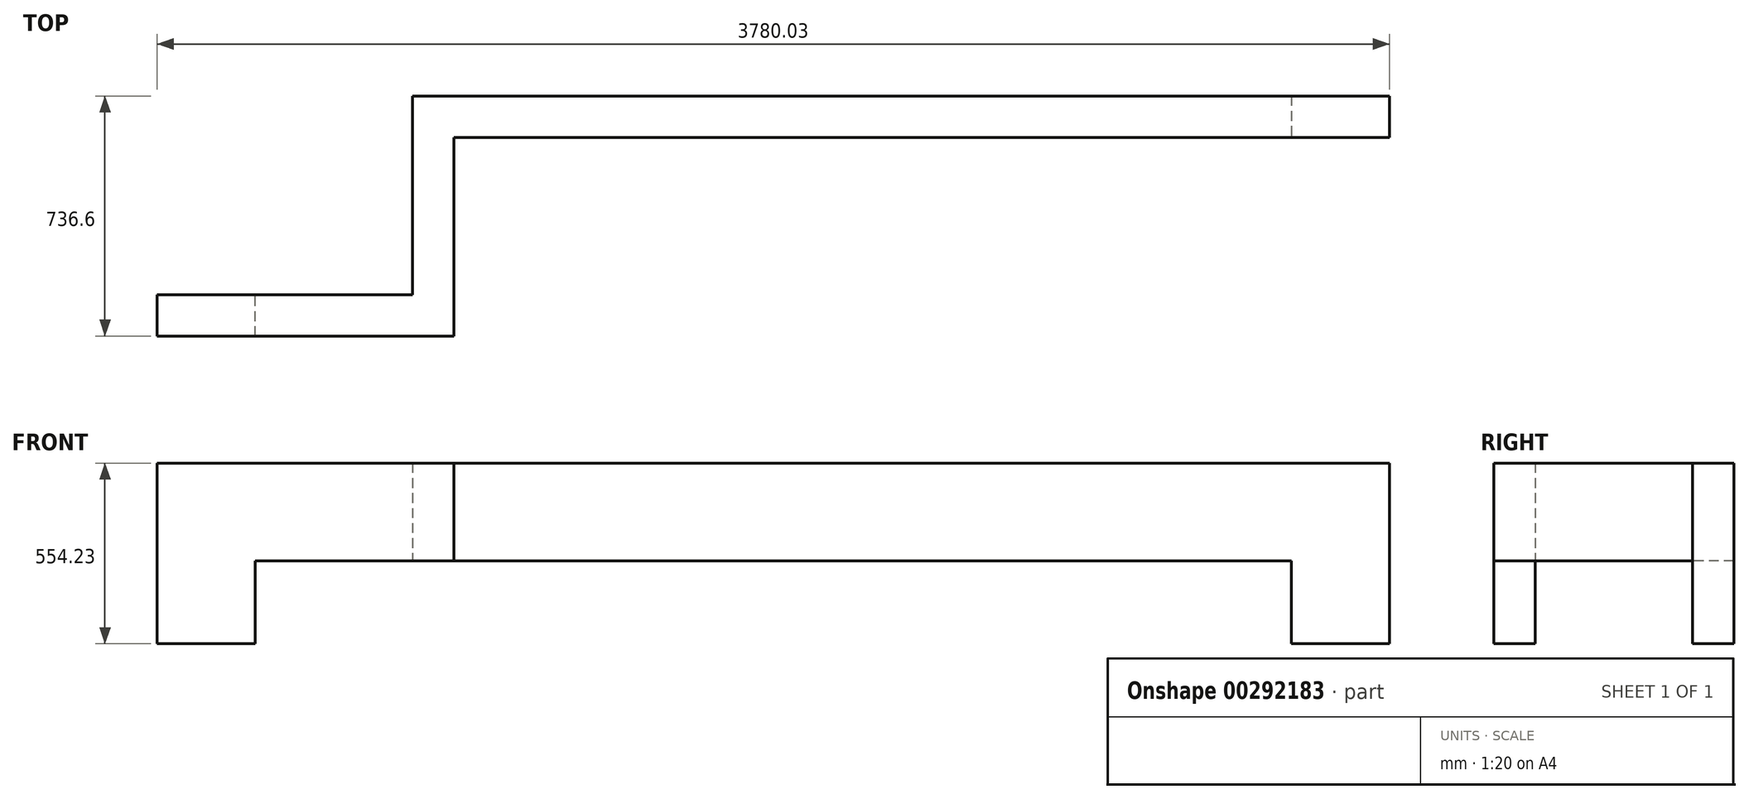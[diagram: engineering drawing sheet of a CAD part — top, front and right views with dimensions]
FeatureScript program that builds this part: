
annotation { "Feature Type Name" : "Feature", "Feature Type Description" : "" }
export const myFeature = defineFeature(function(context is Context, id is Id, definition is map)
    precondition{}
    {
        {
            var Q0;
            Q0=qCreatedBy(makeId("Top.planeOp"),FACE);
            var sketch = newSketch(context, id + "F0", { "sketchPlane" : qUnion([Q0])});
            skLineSegment(sketch, "E0.bottom", {"start": v(0, 0) * mm, "end": v(300.23, 0) * mm});
            skLineSegment(sketch, "E0.top", {"start": v(0, 127) * mm, "end": v(300.23, 127) * mm});
            skLineSegment(sketch, "E0.left", {"start": v(0, 0) * mm, "end": v(0, 127) * mm});
            skLineSegment(sketch, "E0.right", {"start": v(300.23, 0) * mm, "end": v(300.23, 127) * mm});
            skSolve(sketch);
        }
        {
            var Q0;
            Q0=makeQuery(id+"F0.imprint","IMPRINT",FACE,{"disambiguationData":[TD([[makeQuery(id+"F0.imprint","IMPRINT",EDGE,{"derivedFrom":sQuery(id+"F0.wireOp",EDGE,"E0.bottom")}),1.0]])]});
            extrude(context, id + "F1", {"entities" : qUnion([Q0]), "depth" : 254 * mm});
        }
        {
            var Q0;
            Q0=makeQuery(id+"F1.opExtrude","CAP_FACE",FACE,{"disambiguationData":[OSD([sQuery(id+"F0.wireOp",EDGE,"E0.bottom"),sQuery(id+"F0.wireOp",EDGE,"E0.top"),sQuery(id+"F0.wireOp",EDGE,"E0.left"),sQuery(id+"F0.wireOp",EDGE,"E0.right")])],"isStart":false});
            extrude(context, id + "F2", {"entities" : qUnion([Q0]), "operationType" : NewBodyOperationType.ADD, "depth" : 150.11 * mm});
        }
        {
            var Q0;
            Q0=makeQuery(id+"F2.opExtrude","CAP_FACE",FACE,{"disambiguationData":[OSD([sQuery(id+"F0.wireOp",EDGE,"E0.bottom"),sQuery(id+"F0.wireOp",EDGE,"E0.top"),sQuery(id+"F0.wireOp",EDGE,"E0.left"),sQuery(id+"F0.wireOp",EDGE,"E0.right")])],"isStart":false});
            extrude(context, id + "F3", {"entities" : qUnion([Q0]), "operationType" : NewBodyOperationType.ADD, "depth" : 150.11 * mm});
        }
        {
            var Q0;
            {var subQ0=sQuery(id+"F0.wireOp",EDGE,"E0.right");Q0=makeQuery(id+"F3.boolean.opBoolean","MERGE",FACE,{"derivedFrom":[makeQuery(id+"F2.boolean.opBoolean","MERGE",FACE,{"derivedFrom":[makeQuery(id+"F1.opExtrude","SWEPT_FACE",FACE,{"disambiguationData":[OSD([subQ0])]}),makeQuery(id+"F2.opExtrude","SWEPT_FACE",FACE,{"disambiguationData":[OSD([subQ0])]})]}),makeQuery(id+"F3.opExtrude","SWEPT_FACE",FACE,{"disambiguationData":[OSD([subQ0])]})]});}
            var sketch = newSketch(context, id + "F4", { "sketchPlane" : qUnion([Q0])});
            skLineSegment(sketch, "E1.bottom", {"start": v(0, 554.23) * mm, "end": v(127, 554.23) * mm});
            skLineSegment(sketch, "E1.top", {"start": v(0, 254) * mm, "end": v(127, 254) * mm});
            skLineSegment(sketch, "E1.left", {"start": v(0, 554.23) * mm, "end": v(0, 254) * mm});
            skLineSegment(sketch, "E1.right", {"start": v(127, 554.23) * mm, "end": v(127, 254) * mm});
            skSolve(sketch);
        }
        {
            var Q0;
            Q0=makeQuery(id+"F4.imprint","IMPRINT",FACE,{"disambiguationData":[TD([[makeQuery(id+"F4.imprint","IMPRINT",EDGE,{"derivedFrom":sQuery(id+"F4.wireOp",EDGE,"E1.bottom")}),-1.0]])]});
            extrude(context, id + "F5", {"entities" : qUnion([Q0]), "operationType" : NewBodyOperationType.ADD, "depth" : 609.6 * mm});
        }
        {
            var Q0;
            {var subQ0=sQuery(id+"F0.wireOp",EDGE,"E0.top");Q0=makeQuery(id+"F5.boolean.opBoolean","MERGE",FACE,{"derivedFrom":[makeQuery(id+"F3.boolean.opBoolean","MERGE",FACE,{"derivedFrom":[makeQuery(id+"F2.boolean.opBoolean","MERGE",FACE,{"derivedFrom":[makeQuery(id+"F1.opExtrude","SWEPT_FACE",FACE,{"disambiguationData":[OSD([subQ0])]}),makeQuery(id+"F2.opExtrude","SWEPT_FACE",FACE,{"disambiguationData":[OSD([subQ0])]})]}),makeQuery(id+"F3.opExtrude","SWEPT_FACE",FACE,{"disambiguationData":[OSD([subQ0])]})]}),makeQuery(id+"F5.opExtrude","SWEPT_FACE",FACE,{"disambiguationData":[OSD([sQuery(id+"F4.wireOp",EDGE,"E1.right")])]})]});}
            var sketch = newSketch(context, id + "F6", { "sketchPlane" : qUnion([Q0])});
            skLineSegment(sketch, "E2.bottom", {"start": v(-909.83, 554.23) * mm, "end": v(-782.83, 554.23) * mm});
            skLineSegment(sketch, "E2.top", {"start": v(-909.83, 254) * mm, "end": v(-782.83, 254) * mm});
            skLineSegment(sketch, "E2.left", {"start": v(-909.83, 554.23) * mm, "end": v(-909.83, 254) * mm});
            skLineSegment(sketch, "E2.right", {"start": v(-782.83, 554.23) * mm, "end": v(-782.83, 254) * mm});
            skSolve(sketch);
        }
        {
            var Q0;
            Q0=makeQuery(id+"F6.imprint","IMPRINT",FACE,{"disambiguationData":[TD([[makeQuery(id+"F6.imprint","IMPRINT",EDGE,{"derivedFrom":sQuery(id+"F6.wireOp",EDGE,"E2.bottom")}),1.0]])]});
            extrude(context, id + "F7", {"entities" : qUnion([Q0]), "operationType" : NewBodyOperationType.ADD, "depth" : 508 * mm});
        }
        {
            var Q0;
            Q0=makeQuery(id+"F7.boolean.opBoolean","MERGE",FACE,{"derivedFrom":[makeQuery(id+"F5.opExtrude","CAP_FACE",FACE,{"disambiguationData":[OSD([sQuery(id+"F4.wireOp",EDGE,"E1.bottom"),sQuery(id+"F4.wireOp",EDGE,"E1.top"),sQuery(id+"F4.wireOp",EDGE,"E1.left"),sQuery(id+"F4.wireOp",EDGE,"E1.right")])],"isStart":false}),makeQuery(id+"F7.opExtrude","SWEPT_FACE",FACE,{"disambiguationData":[OSD([sQuery(id+"F6.wireOp",EDGE,"E2.left")])]})]});
            var sketch = newSketch(context, id + "F8", { "sketchPlane" : qUnion([Q0])});
            skLineSegment(sketch, "E3.bottom", {"start": v(635, 554.23) * mm, "end": v(508, 554.23) * mm});
            skLineSegment(sketch, "E3.top", {"start": v(635, 254) * mm, "end": v(508, 254) * mm});
            skLineSegment(sketch, "E3.left", {"start": v(635, 554.23) * mm, "end": v(635, 254) * mm});
            skLineSegment(sketch, "E3.right", {"start": v(508, 554.23) * mm, "end": v(508, 254) * mm});
            skSolve(sketch);
        }
        {
            var Q0;
            Q0=makeQuery(id+"F8.imprint","IMPRINT",FACE,{"disambiguationData":[TD([[makeQuery(id+"F8.imprint","IMPRINT",EDGE,{"derivedFrom":sQuery(id+"F8.wireOp",EDGE,"E3.bottom")}),-1.0]])]});
            extrude(context, id + "F9", {"entities" : qUnion([Q0]), "operationType" : NewBodyOperationType.ADD, "depth" : 1524 * mm});
        }
        {
            var Q0;
            Q0=makeQuery(id+"F9.opExtrude","CAP_FACE",FACE,{"disambiguationData":[OSD([sQuery(id+"F8.wireOp",EDGE,"E3.bottom"),sQuery(id+"F8.wireOp",EDGE,"E3.top"),sQuery(id+"F8.wireOp",EDGE,"E3.left"),sQuery(id+"F8.wireOp",EDGE,"E3.right")])],"isStart":false});
            extrude(context, id + "F10", {"entities" : qUnion([Q0]), "operationType" : NewBodyOperationType.ADD, "depth" : 694.5 * mm});
        }
        {
            var Q0;
            Q0=makeQuery(id+"F10.opExtrude","CAP_FACE",FACE,{"disambiguationData":[OSD([sQuery(id+"F8.wireOp",EDGE,"E3.bottom"),sQuery(id+"F8.wireOp",EDGE,"E3.top"),sQuery(id+"F8.wireOp",EDGE,"E3.left"),sQuery(id+"F8.wireOp",EDGE,"E3.right")])],"isStart":false});
            extrude(context, id + "F11", {"entities" : qUnion([Q0]), "operationType" : NewBodyOperationType.ADD, "depth" : 150.11 * mm});
        }
        {
            var Q0;
            {var subQ0=sQuery(id+"F8.wireOp",EDGE,"E3.top");Q0=makeQuery(id+"F11.boolean.opBoolean","MERGE",FACE,{"derivedFrom":[makeQuery(id+"F10.boolean.opBoolean","MERGE",FACE,{"derivedFrom":[makeQuery(id+"F9.boolean.opBoolean","MERGE",FACE,{"derivedFrom":[makeQuery(id+"F7.boolean.opBoolean","MERGE",FACE,{"derivedFrom":[makeQuery(id+"F5.opExtrude","SWEPT_FACE",FACE,{"disambiguationData":[OSD([sQuery(id+"F4.wireOp",EDGE,"E1.top")])]}),makeQuery(id+"F7.opExtrude","SWEPT_FACE",FACE,{"disambiguationData":[OSD([sQuery(id+"F6.wireOp",EDGE,"E2.top")])]})]}),makeQuery(id+"F9.opExtrude","SWEPT_FACE",FACE,{"disambiguationData":[OSD([subQ0])]})]}),makeQuery(id+"F10.opExtrude","SWEPT_FACE",FACE,{"disambiguationData":[OSD([subQ0])]})]}),makeQuery(id+"F11.opExtrude","SWEPT_FACE",FACE,{"disambiguationData":[OSD([subQ0])]})]});}
            var sketch = newSketch(context, id + "F12", { "sketchPlane" : qUnion([Q0])});
            skLineSegment(sketch, "E4.bottom", {"start": v(3278.45, -635) * mm, "end": v(2978.23, -635) * mm});
            skLineSegment(sketch, "E4.top", {"start": v(3278.45, -508) * mm, "end": v(2978.23, -508) * mm});
            skLineSegment(sketch, "E4.left", {"start": v(3278.45, -635) * mm, "end": v(3278.45, -508) * mm});
            skLineSegment(sketch, "E4.right", {"start": v(2978.23, -635) * mm, "end": v(2978.23, -508) * mm});
            skSolve(sketch);
        }
        {
            var Q0;
            Q0=makeQuery(id+"F12.imprint","IMPRINT",FACE,{"disambiguationData":[TD([[makeQuery(id+"F12.imprint","IMPRINT",EDGE,{"derivedFrom":sQuery(id+"F12.wireOp",EDGE,"E4.bottom")}),-1.0]])]});
            extrude(context, id + "F13", {"entities" : qUnion([Q0]), "operationType" : NewBodyOperationType.ADD, "depth" : 254 * mm});
        }
        {
            var Q0;
            {var subQ0=sQuery(id+"F8.wireOp",EDGE,"E3.left");Q0=makeQuery(id+"F13.boolean.opBoolean","MERGE",FACE,{"derivedFrom":[makeQuery(id+"F11.boolean.opBoolean","MERGE",FACE,{"derivedFrom":[makeQuery(id+"F10.boolean.opBoolean","MERGE",FACE,{"derivedFrom":[makeQuery(id+"F9.boolean.opBoolean","MERGE",FACE,{"derivedFrom":[makeQuery(id+"F7.opExtrude","CAP_FACE",FACE,{"disambiguationData":[OSD([sQuery(id+"F6.wireOp",EDGE,"E2.bottom"),sQuery(id+"F6.wireOp",EDGE,"E2.top"),sQuery(id+"F6.wireOp",EDGE,"E2.left"),sQuery(id+"F6.wireOp",EDGE,"E2.right")])],"isStart":false}),makeQuery(id+"F9.opExtrude","SWEPT_FACE",FACE,{"disambiguationData":[OSD([subQ0])]})]}),makeQuery(id+"F10.opExtrude","SWEPT_FACE",FACE,{"disambiguationData":[OSD([subQ0])]})]}),makeQuery(id+"F11.opExtrude","SWEPT_FACE",FACE,{"disambiguationData":[OSD([subQ0])]})]}),makeQuery(id+"F13.opExtrude","SWEPT_FACE",FACE,{"disambiguationData":[OSD([sQuery(id+"F12.wireOp",EDGE,"E4.bottom")])]})]});}
            extrude(context, id + "F14", {"entities" : qUnion([Q0]), "operationType" : NewBodyOperationType.ADD, "depth" : 101.6 * mm});
        }
        {
            var Q0;
            {var subQ0=sQuery(id+"F8.wireOp",EDGE,"E3.right");Q0=makeQuery(id+"F13.boolean.opBoolean","MERGE",FACE,{"derivedFrom":[makeQuery(id+"F11.boolean.opBoolean","MERGE",FACE,{"derivedFrom":[makeQuery(id+"F10.boolean.opBoolean","MERGE",FACE,{"derivedFrom":[makeQuery(id+"F9.opExtrude","SWEPT_FACE",FACE,{"disambiguationData":[OSD([subQ0])]}),makeQuery(id+"F10.opExtrude","SWEPT_FACE",FACE,{"disambiguationData":[OSD([subQ0])]})]}),makeQuery(id+"F11.opExtrude","SWEPT_FACE",FACE,{"disambiguationData":[OSD([subQ0])]})]}),makeQuery(id+"F13.opExtrude","SWEPT_FACE",FACE,{"disambiguationData":[OSD([sQuery(id+"F12.wireOp",EDGE,"E4.top")])]})]});}
            extrude(context, id + "F15", {"entities" : qUnion([Q0]), "operationType" : NewBodyOperationType.REMOVE, "oppositeDirection" : true, "depth" : 101.6 * mm});
        }
        {
            var Q0;
            {var subQ0=sQuery(id+"F12.wireOp",EDGE,"E4.left");var subQ1=sQuery(id+"F8.wireOp",EDGE,"E3.left");Q0=makeQuery(id+"F14.boolean.opBoolean","MERGE",FACE,{"derivedFrom":[makeQuery(id+"F13.boolean.opBoolean","MERGE",FACE,{"derivedFrom":[makeQuery(id+"F11.opExtrude","CAP_FACE",FACE,{"disambiguationData":[OSD([sQuery(id+"F8.wireOp",EDGE,"E3.bottom"),sQuery(id+"F8.wireOp",EDGE,"E3.top"),subQ1,sQuery(id+"F8.wireOp",EDGE,"E3.right")])],"isStart":false}),makeQuery(id+"F13.opExtrude","SWEPT_FACE",FACE,{"disambiguationData":[OSD([subQ0])]})]}),makeQuery(id+"F14.opExtrude","SWEPT_FACE",FACE,{"disambiguationData":[OSD([subQ1,sQuery(id+"F12.wireOp",EDGE,"E4.bottom"),subQ0])]})]});}
            extrude(context, id + "F16", {"entities" : qUnion([Q0]), "operationType" : NewBodyOperationType.ADD, "depth" : 438.07 * mm});
        }
        {
            var Q0;
            {var subQ0=sQuery(id+"F12.wireOp",EDGE,"E4.right");Q0=makeQuery(id+"F14.boolean.opBoolean","MERGE",FACE,{"derivedFrom":[makeQuery(id+"F13.opExtrude","SWEPT_FACE",FACE,{"disambiguationData":[OSD([subQ0])]}),makeQuery(id+"F14.opExtrude","SWEPT_FACE",FACE,{"disambiguationData":[OSD([sQuery(id+"F6.wireOp",EDGE,"E2.top"),sQuery(id+"F8.wireOp",EDGE,"E3.top"),sQuery(id+"F8.wireOp",EDGE,"E3.left"),sQuery(id+"F12.wireOp",EDGE,"E4.bottom"),subQ0])]})]});}
            extrude(context, id + "F17", {"entities" : qUnion([Q0]), "operationType" : NewBodyOperationType.REMOVE, "oppositeDirection" : true, "depth" : 438.07 * mm});
        }
        {
            var Q0;
            Q0=makeQuery(id+"F16.opExtrude","CAP_FACE",FACE,{"disambiguationData":[OSD([sQuery(id+"F8.wireOp",EDGE,"E3.bottom"),sQuery(id+"F8.wireOp",EDGE,"E3.top"),sQuery(id+"F8.wireOp",EDGE,"E3.left"),sQuery(id+"F8.wireOp",EDGE,"E3.right"),sQuery(id+"F12.wireOp",EDGE,"E4.bottom"),sQuery(id+"F12.wireOp",EDGE,"E4.left")])],"isStart":false});
            extrude(context, id + "F18", {"entities" : qUnion([Q0]), "operationType" : NewBodyOperationType.ADD, "depth" : 76.2 * mm});
        }
        {
            var Q0;
            Q0=makeQuery(id+"F17.boolean.opBoolean","COPY",FACE,{"derivedFrom":makeQuery(id+"F17.opExtrude","CAP_FACE",FACE,{"disambiguationData":[OSD([sQuery(id+"F6.wireOp",EDGE,"E2.top"),sQuery(id+"F8.wireOp",EDGE,"E3.top"),sQuery(id+"F8.wireOp",EDGE,"E3.left"),sQuery(id+"F12.wireOp",EDGE,"E4.bottom"),sQuery(id+"F12.wireOp",EDGE,"E4.right")])],"isStart":false})});
            extrude(context, id + "F19", {"entities" : qUnion([Q0]), "operationType" : NewBodyOperationType.REMOVE, "oppositeDirection" : true, "depth" : 76.2 * mm});
        }
        {
            var Q0;
            Q0=makeQuery(id+"F19.boolean.opBoolean","COPY",FACE,{"derivedFrom":makeQuery(id+"F19.opExtrude","CAP_FACE",FACE,{"disambiguationData":[OSD([sQuery(id+"F6.wireOp",EDGE,"E2.top"),sQuery(id+"F8.wireOp",EDGE,"E3.top"),sQuery(id+"F8.wireOp",EDGE,"E3.left"),sQuery(id+"F12.wireOp",EDGE,"E4.bottom"),sQuery(id+"F12.wireOp",EDGE,"E4.right")])],"isStart":false})});
            extrude(context, id + "F20", {"entities" : qUnion([Q0]), "operationType" : NewBodyOperationType.ADD, "depth" : 12.7 * mm});
        }
        {
            var Q0;
            Q0=makeQuery(id+"F18.opExtrude","CAP_FACE",FACE,{"disambiguationData":[OSD([sQuery(id+"F8.wireOp",EDGE,"E3.bottom"),sQuery(id+"F8.wireOp",EDGE,"E3.top"),sQuery(id+"F8.wireOp",EDGE,"E3.left"),sQuery(id+"F8.wireOp",EDGE,"E3.right"),sQuery(id+"F12.wireOp",EDGE,"E4.bottom"),sQuery(id+"F12.wireOp",EDGE,"E4.left")])],"isStart":false});
            extrude(context, id + "F21", {"entities" : qUnion([Q0]), "operationType" : NewBodyOperationType.REMOVE, "oppositeDirection" : true, "depth" : 12.7 * mm});
        }
    });
